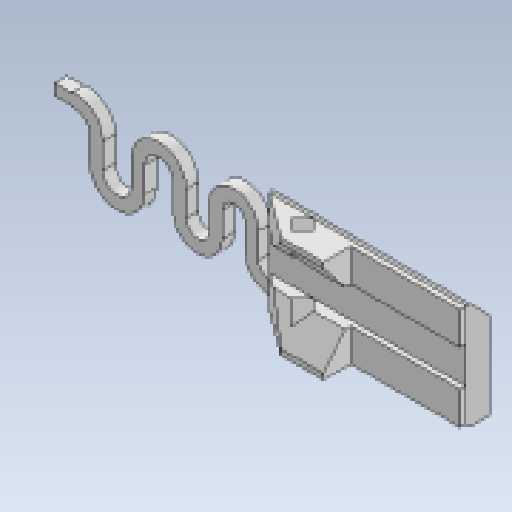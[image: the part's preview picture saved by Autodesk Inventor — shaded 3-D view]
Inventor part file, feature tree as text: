
AUTODESK INVENTOR PART (.ipt)
format: ipt  version: 2023 (Build 270158030, 158C)  size: 210,432 bytes
history: native  units: mm
features: other x7, chamfer x1, extrude x1, sketch x1, reference x1, projected_geometry x1
ambient origin geometry x8: Origin, YZ Plane, XZ Plane, XY Plane, X Axis, Y Axis, Z Axis, Center Point
bodies: Body1 (feature_tree)
feature tree (12):
  other  "v4-latch.ipt"
  chamfer  "Chamfer1"  Distance=0.15mm Angle=45.0deg
  extrude  "Extrusion1"  TaperAngle=0.0deg  [1 undecoded]
  other  "slide::v4-latch.ipt"
  other  "TaggingFeature1"
  sketch  "Sketch1"  dims[d0=10.0mm d1=0.15mm d2=2.0mm d3=45.0deg d4=0.0mm d5=0.0mm]
  reference  "Reference1"
  projected_geometry  "Projected Loop1"
  other  "slide"
  other  "<userpath>\Documents\0004-inventor\3D-CAD-main\trebuchet\V4.0-trebuchet-printable.iam"
  other  "V4.0-trebuchet-printable.iam"
  other  "border:1"
note: 1 required parameter value undecoded (feature->parameter linkage not recoverable at this tier; creation-order binding heuristic only, values carry confidence <= 0.55)
